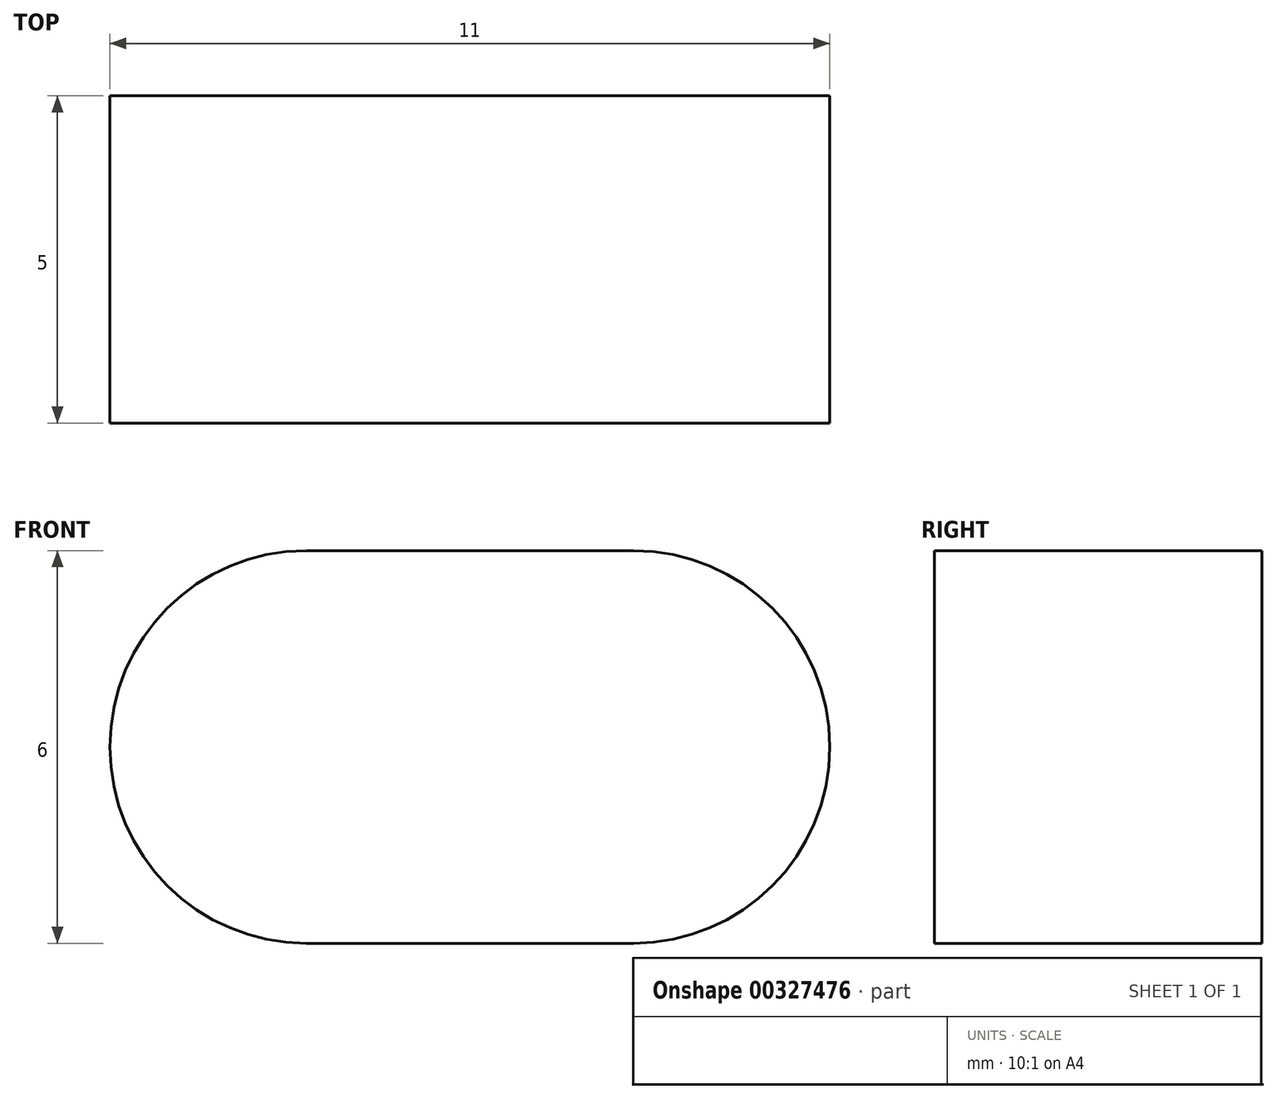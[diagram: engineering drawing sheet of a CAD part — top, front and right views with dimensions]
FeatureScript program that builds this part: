
annotation { "Feature Type Name" : "Feature", "Feature Type Description" : "" }
export const myFeature = defineFeature(function(context is Context, id is Id, definition is map)
    precondition{}
    {
        {
            var Q0;
            Q0=qCreatedBy(makeId("Front.planeOp"),FACE);
            var sketch = newSketch(context, id + "F0", { "sketchPlane" : qUnion([Q0])});
            skLineSegment(sketch, "E0.bottom", {"start": v(2.5, 3) * mm, "end": v(-2.5, 3) * mm});
            skLineSegment(sketch, "E0.top", {"start": v(2.5, -3) * mm, "end": v(-2.5, -3) * mm});
            skLineSegment(sketch, "E0.left", {"start": v(2.5, 3) * mm, "end": v(2.5, -3) * mm});
            skLineSegment(sketch, "E0.right", {"start": v(-2.5, 3) * mm, "end": v(-2.5, -3) * mm});
            skPoint(sketch, "E0.middle", {"position": v(0, 0) * mm});
            skArc(sketch, "E1", {"start": v(2.5, -3) * mm, "mid": v(5.5, 0) * mm, "end": v(2.5, 3) * mm});
            skArc(sketch, "E2", {"start": v(-2.5, 3) * mm, "mid": v(-5.5, 0) * mm, "end": v(-2.5, -3) * mm});
            skSolve(sketch);
        }
        {
            var Q0;
            Q0 = qSketchRegion(id + "F0", true);
            extrude(context, id + "F1", {"entities" : qUnion([Q0]), "depth" : 5 * mm});
        }
    });
